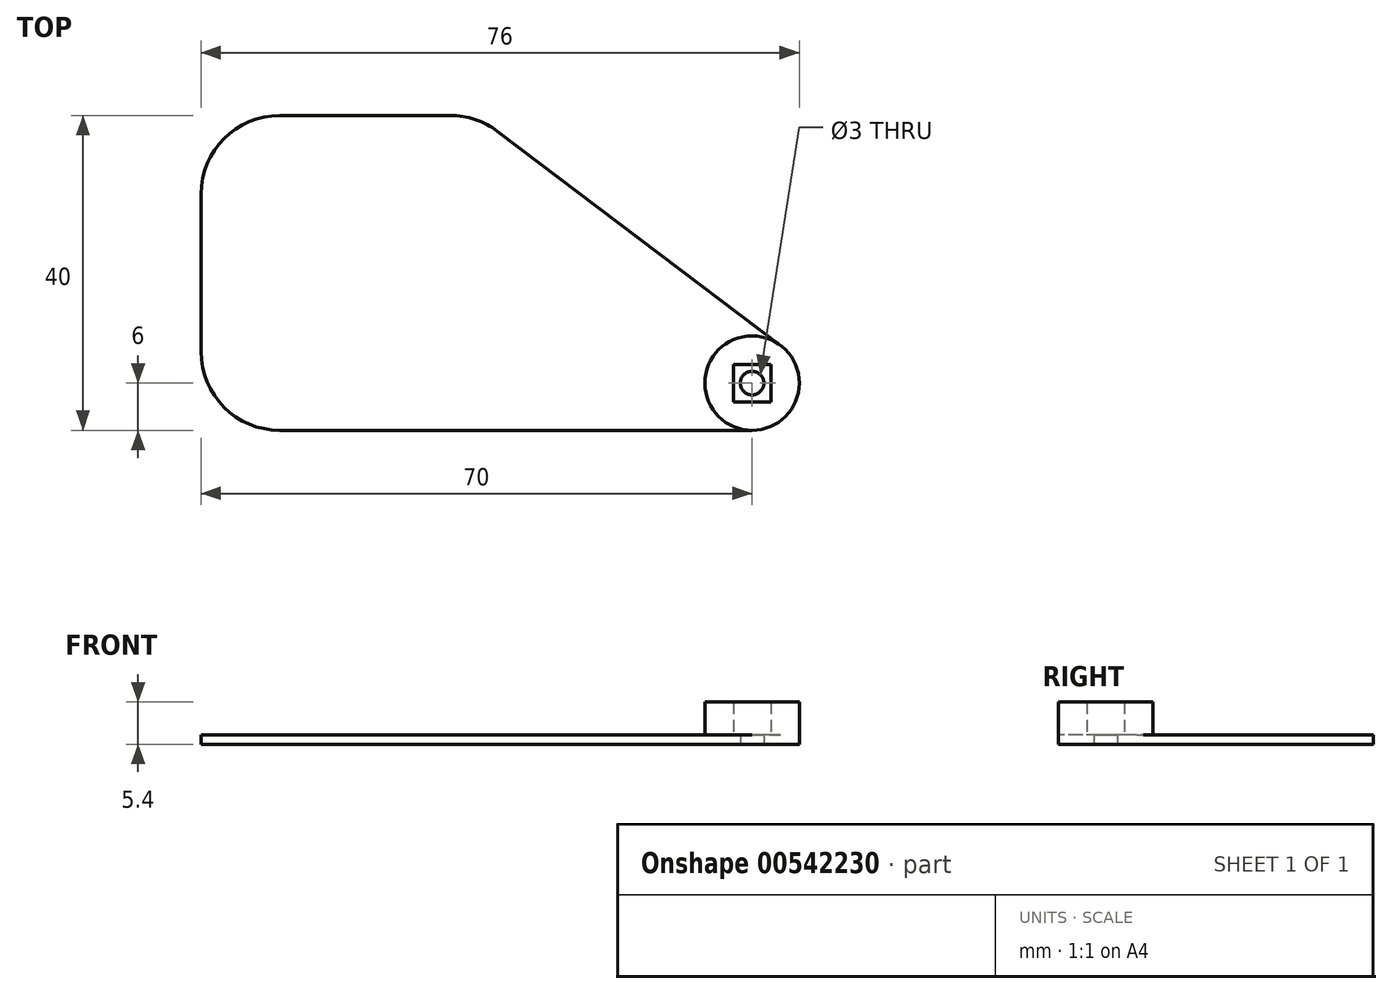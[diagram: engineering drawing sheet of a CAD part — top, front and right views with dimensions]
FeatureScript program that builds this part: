
annotation { "Feature Type Name" : "Feature", "Feature Type Description" : "" }
export const myFeature = defineFeature(function(context is Context, id is Id, definition is map)
    precondition{}
    {
        {
            var Q0;
            Q0=qCreatedBy(makeId("Top.planeOp"),FACE);
            var sketch = newSketch(context, id + "F0", { "sketchPlane" : qUnion([Q0])});
            skArc(sketch, "E0", {"start": v(0, -6) * mm, "mid": v(5.69, -1.9) * mm, "end": v(3.62, 4.79) * mm});
            skLineSegment(sketch, "E1.bottom", {"start": v(2.38, 2.38) * mm, "end": v(-2.38, 2.38) * mm});
            skLineSegment(sketch, "E1.top", {"start": v(2.38, -2.38) * mm, "end": v(-2.38, -2.38) * mm});
            skLineSegment(sketch, "E1.left", {"start": v(2.38, 2.38) * mm, "end": v(2.38, -2.38) * mm});
            skLineSegment(sketch, "E1.right", {"start": v(-2.38, 2.38) * mm, "end": v(-2.38, -2.38) * mm});
            skLineSegment(sketch, "E2", {"start": v(0, -6) * mm, "end": v(-60, -6) * mm});
            skLineSegment(sketch, "E3", {"start": v(-70, 4) * mm, "end": v(-70, 24) * mm});
            skLineSegment(sketch, "E4", {"start": v(-60, 34) * mm, "end": v(-38.36, 34) * mm});
            skLineSegment(sketch, "E5", {"start": v(-32.32, 31.98) * mm, "end": v(3.62, 4.79) * mm});
            skPoint(sketch, "E6.visualSharp", {"position": v(-70, 34) * mm});
            skArc(sketch, "E6.filletArc", {"start": v(-60, 34) * mm, "mid": v(-67.07, 31.07) * mm, "end": v(-70, 24) * mm});
            skPoint(sketch, "E7.visualSharp", {"position": v(-70, -6) * mm});
            skArc(sketch, "E7.filletArc", {"start": v(-70, 4) * mm, "mid": v(-67.07, -3.07) * mm, "end": v(-60, -6) * mm});
            skPoint(sketch, "E8.visualSharp", {"position": v(-35, 34) * mm});
            skArc(sketch, "E8.filletArc", {"start": v(-32.32, 31.98) * mm, "mid": v(-35.17, 33.48) * mm, "end": v(-38.36, 34) * mm});
            skSolve(sketch);
        }
        {
            var Q0;
            Q0 = qSketchRegion(id + "F0", true);
            extrude(context, id + "F1", {"entities" : qUnion([Q0]), "depth" : 1.2 * mm, "offsetDistance" : 25 * mm});
        }
        {
            var Q0;
            Q0=makeQuery(id+"F1.opExtrude","CAP_FACE",FACE,{"disambiguationData":[OSD([sQuery(id+"F0.wireOp",EDGE,"E0"),sQuery(id+"F0.wireOp",EDGE,"E1.bottom"),sQuery(id+"F0.wireOp",EDGE,"E1.top"),sQuery(id+"F0.wireOp",EDGE,"E1.left"),sQuery(id+"F0.wireOp",EDGE,"E1.right"),sQuery(id+"F0.wireOp",EDGE,"E2"),sQuery(id+"F0.wireOp",EDGE,"E3"),sQuery(id+"F0.wireOp",EDGE,"E4"),sQuery(id+"F0.wireOp",EDGE,"E5"),sQuery(id+"F0.wireOp",EDGE,"E6.filletArc"),sQuery(id+"F0.wireOp",EDGE,"E7.filletArc"),sQuery(id+"F0.wireOp",EDGE,"E8.filletArc")])],"isStart":false});
            var sketch = newSketch(context, id + "F2", { "sketchPlane" : qUnion([Q0])});
            skCircle(sketch, "E9", {"center": v(0, 0) * mm, "radius": 6 * mm});
            skLineSegment(sketch, "E10.bottom", {"start": v(2.38, 2.38) * mm, "end": v(-2.38, 2.38) * mm});
            skLineSegment(sketch, "E10.top", {"start": v(2.38, -2.38) * mm, "end": v(-2.38, -2.38) * mm});
            skLineSegment(sketch, "E10.left", {"start": v(2.38, 2.38) * mm, "end": v(2.38, -2.38) * mm});
            skLineSegment(sketch, "E10.right", {"start": v(-2.38, 2.38) * mm, "end": v(-2.38, -2.38) * mm});
            skSolve(sketch);
        }
        {
            var Q0;
            Q0 = qSketchRegion(id + "F2", true);
            extrude(context, id + "F3", {"entities" : qUnion([Q0]), "operationType" : NewBodyOperationType.ADD, "depth" : 4.2 * mm, "offsetDistance" : 25 * mm});
        }
        {
            var Q0;
            Q0=makeQuery(id+"F1.opExtrude","CAP_FACE",FACE,{"disambiguationData":[OSD([sQuery(id+"F0.wireOp",EDGE,"E0"),sQuery(id+"F0.wireOp",EDGE,"E1.bottom"),sQuery(id+"F0.wireOp",EDGE,"E1.top"),sQuery(id+"F0.wireOp",EDGE,"E1.left"),sQuery(id+"F0.wireOp",EDGE,"E1.right"),sQuery(id+"F0.wireOp",EDGE,"E2"),sQuery(id+"F0.wireOp",EDGE,"E3"),sQuery(id+"F0.wireOp",EDGE,"E4"),sQuery(id+"F0.wireOp",EDGE,"E5"),sQuery(id+"F0.wireOp",EDGE,"E6.filletArc"),sQuery(id+"F0.wireOp",EDGE,"E7.filletArc"),sQuery(id+"F0.wireOp",EDGE,"E8.filletArc")])],"isStart":true});
            var sketch = newSketch(context, id + "F4", { "sketchPlane" : qUnion([Q0])});
            skCircle(sketch, "E11", {"center": v(0, 0) * mm, "radius": 1.5 * mm});
            skLineSegment(sketch, "E12.bottom", {"start": v(2.38, 2.38) * mm, "end": v(-2.38, 2.38) * mm});
            skLineSegment(sketch, "E12.top", {"start": v(2.38, -2.38) * mm, "end": v(-2.38, -2.38) * mm});
            skLineSegment(sketch, "E12.left", {"start": v(2.38, 2.38) * mm, "end": v(2.38, -2.38) * mm});
            skLineSegment(sketch, "E12.right", {"start": v(-2.38, 2.38) * mm, "end": v(-2.38, -2.38) * mm});
            skSolve(sketch);
        }
        {
            var Q0;
            Q0 = qSketchRegion(id + "F4", true);
            extrude(context, id + "F5", {"entities" : qUnion([Q0]), "operationType" : NewBodyOperationType.ADD, "oppositeDirection" : true, "depth" : 1.2 * mm, "offsetDistance" : 25 * mm});
        }
    });
